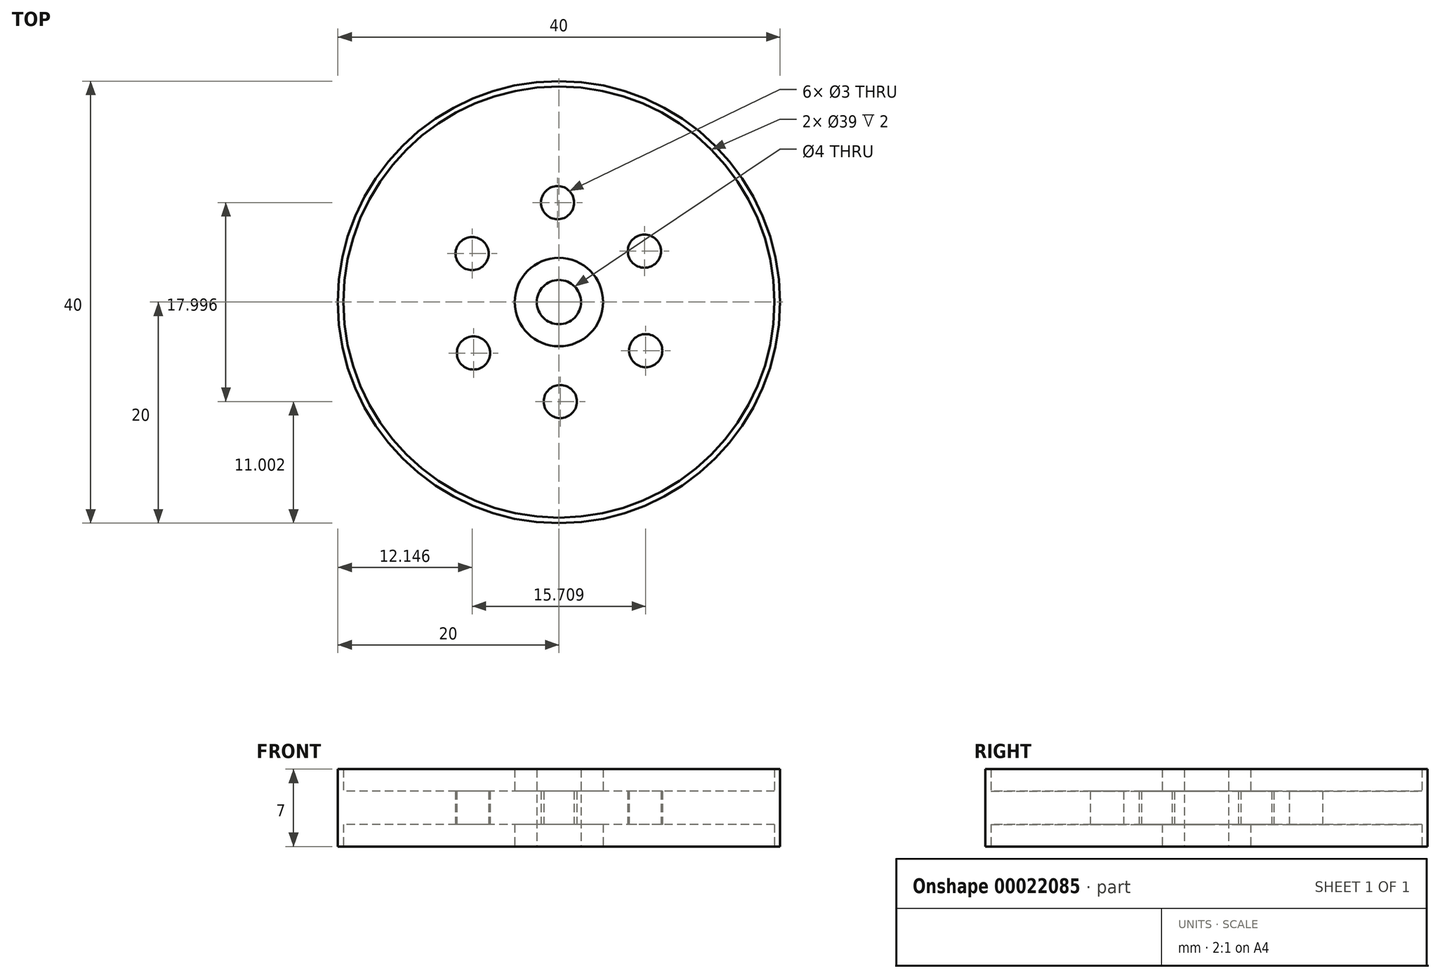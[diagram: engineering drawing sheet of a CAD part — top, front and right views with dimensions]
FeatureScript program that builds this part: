
annotation { "Feature Type Name" : "Feature", "Feature Type Description" : "" }
export const myFeature = defineFeature(function(context is Context, id is Id, definition is map)
    precondition{}
    {
        {
            var Q0;
            Q0=qCreatedBy(makeId("Top.planeOp"),FACE);
            var sketch = newSketch(context, id + "F0", { "sketchPlane" : qUnion([Q0])});
            skCircle(sketch, "E0", {"center": v(0, 0) * mm, "radius": 20 * mm});
            skPoint(sketch, "E1.orphan", {"position": v(-20, 0) * mm});
            skCircle(sketch, "E2", {"center": v(0, 0) * mm, "radius": 19.5 * mm});
            skCircle(sketch, "E3", {"center": v(0, 0) * mm, "radius": 4 * mm});
            skCircle(sketch, "E4", {"center": v(0, 0) * mm, "radius": 2 * mm});
            skCircle(sketch, "E5", {"center": v(-0.12, 9) * mm, "radius": 1.5 * mm});
            skCircle(sketch, "E6.1.0", {"center": v(-7.85, 4.4) * mm, "radius": 1.5 * mm});
            skCircle(sketch, "E6.2.0", {"center": v(-7.73, -4.6) * mm, "radius": 1.5 * mm});
            skCircle(sketch, "E6.3.0", {"center": v(0.12, -9) * mm, "radius": 1.5 * mm});
            skCircle(sketch, "E6.4.0", {"center": v(7.85, -4.4) * mm, "radius": 1.5 * mm});
            skCircle(sketch, "E6.5.0", {"center": v(7.73, 4.6) * mm, "radius": 1.5 * mm});
            skSolve(sketch);
        }
        {
            var Q0;
            Q0=makeQuery(id+"F0.imprint","IMPRINT",FACE,{"disambiguationData":[TD([[makeQuery(id+"F0.imprint","IMPRINT",EDGE,{"derivedFrom":sQuery(id+"F0.wireOp",EDGE,"E0")}),1.0]])]});
            extrude(context, id + "F1", {"entities" : qUnion([Q0]), "endBound" : BoundingType.SYMMETRIC, "depth" : 7 * mm});
        }
        {
            var Q0;
            Q0=makeQuery(id+"F0.imprint","IMPRINT",FACE,{"disambiguationData":[TD([[makeQuery(id+"F0.imprint","IMPRINT",EDGE,{"derivedFrom":sQuery(id+"F0.wireOp",EDGE,"E2")}),1.0]])]});
            extrude(context, id + "F2", {"entities" : qUnion([Q0]), "operationType" : NewBodyOperationType.ADD, "endBound" : BoundingType.SYMMETRIC, "depth" : 3 * mm});
        }
        {
            var Q0;
            Q0=makeQuery(id+"F0.imprint","IMPRINT",FACE,{"disambiguationData":[TD([[makeQuery(id+"F0.imprint","IMPRINT",EDGE,{"derivedFrom":sQuery(id+"F0.wireOp",EDGE,"E3")}),1.0]])]});
            extrude(context, id + "F3", {"entities" : qUnion([Q0]), "operationType" : NewBodyOperationType.ADD, "endBound" : BoundingType.SYMMETRIC, "depth" : 7 * mm});
        }
    });
